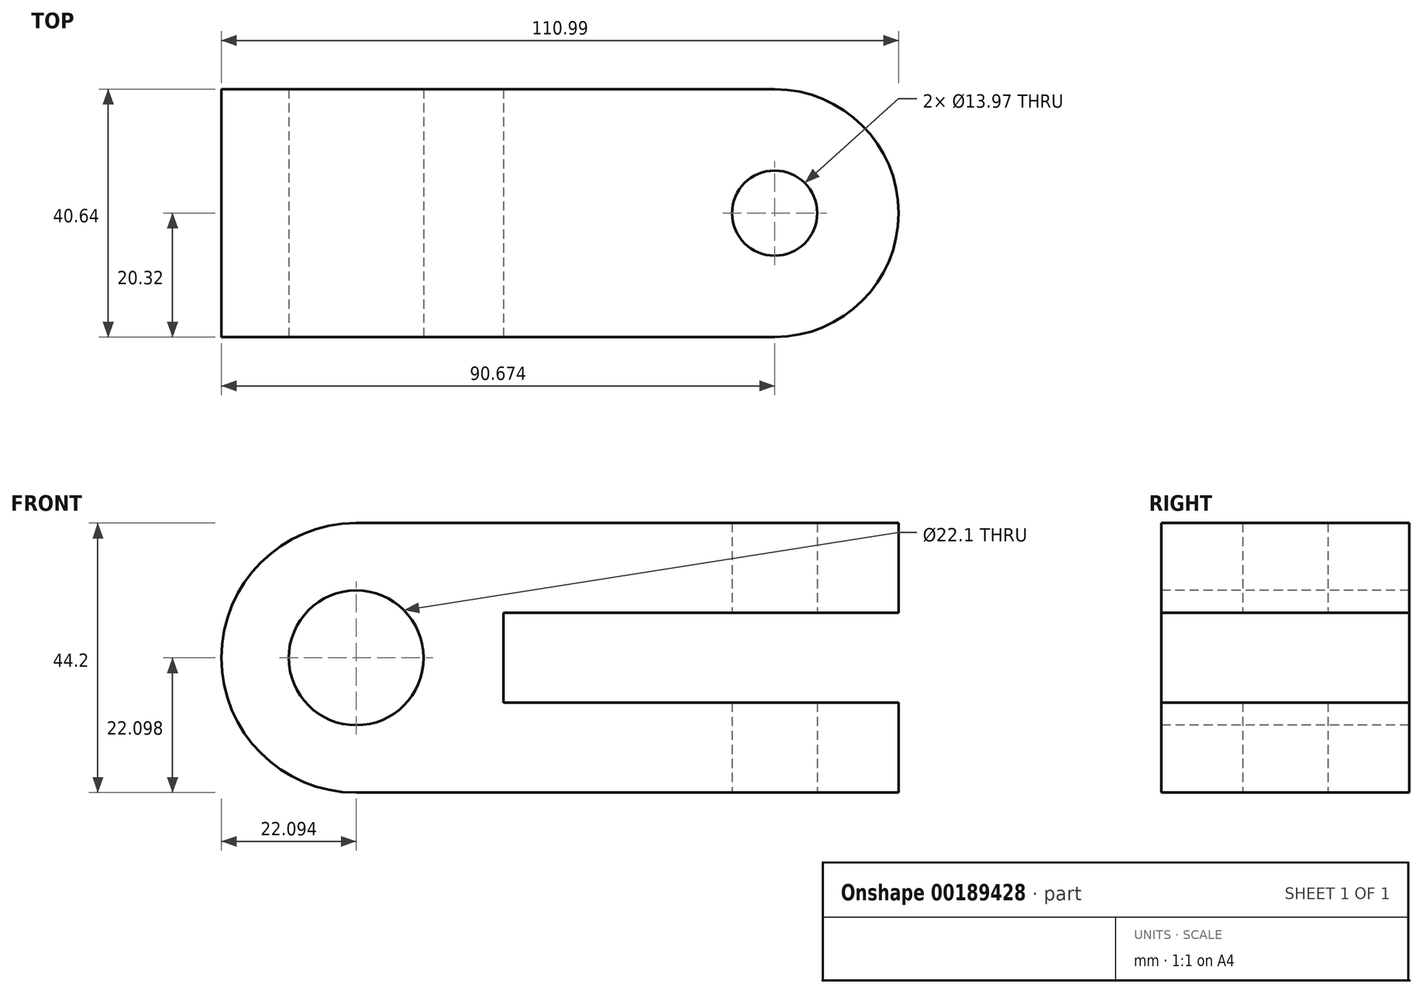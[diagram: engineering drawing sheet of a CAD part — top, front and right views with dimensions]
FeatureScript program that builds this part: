
annotation { "Feature Type Name" : "Feature", "Feature Type Description" : "" }
export const myFeature = defineFeature(function(context is Context, id is Id, definition is map)
    precondition{}
    {
        {
            var Q0;
            Q0=qCreatedBy(makeId("Top.planeOp"),FACE);
            var sketch = newSketch(context, id + "F0", { "sketchPlane" : qUnion([Q0])});
            skLineSegment(sketch, "E0.bottom", {"start": v(-36.36, 20.32) * mm, "end": v(32.22, 20.32) * mm});
            skLineSegment(sketch, "E0.top", {"start": v(-36.36, -20.32) * mm, "end": v(32.22, -20.32) * mm});
            skLineSegment(sketch, "E0.left", {"start": v(-36.36, 20.32) * mm, "end": v(-36.36, -20.32) * mm});
            skLineSegment(sketch, "E0.right", {"start": v(32.22, 20.32) * mm, "end": v(32.22, -20.32) * mm});
            skPoint(sketch, "E0.middle", {"position": v(-2.07, 0) * mm});
            skArc(sketch, "E1", {"start": v(32.22, -20.32) * mm, "mid": v(52.54, 0) * mm, "end": v(32.22, 20.32) * mm});
            skCircle(sketch, "E2", {"center": v(32.22, 0) * mm, "radius": 6.99 * mm});
            skSolve(sketch);
        }
        {
            var Q0;
            Q0=qCreatedBy(makeId("Front.planeOp"),FACE);
            var sketch = newSketch(context, id + "F1", { "sketchPlane" : qUnion([Q0])});
            skLineSegment(sketch, "E3.bottom", {"start": v(52.54, 29.46) * mm, "end": v(-12.23, 29.46) * mm});
            skLineSegment(sketch, "E3.top", {"start": v(52.54, 14.73) * mm, "end": v(-12.23, 14.73) * mm});
            skLineSegment(sketch, "E3.left", {"start": v(52.54, 29.46) * mm, "end": v(52.54, 14.73) * mm});
            skLineSegment(sketch, "E3.right", {"start": v(-12.23, 29.46) * mm, "end": v(-12.23, 14.73) * mm});
            skSolve(sketch);
        }
        {
            var Q0;
            Q0=qCreatedBy(makeId("Front.planeOp"),FACE);
            var sketch = newSketch(context, id + "F2", { "sketchPlane" : qUnion([Q0])});
            skCircle(sketch, "E4", {"center": v(-36.36, 22.1) * mm, "radius": 11.05 * mm});
            skCircle(sketch, "E5.0", {"center": v(-36.36, 22.1) * mm, "radius": 22.1 * mm});
            skSolve(sketch);
        }
        {
            var Q0;
            {var subQ2=sQuery(id+"F0.wireOp",EDGE,"E0.bottom");Q0=makeQuery(id+"F0.imprint","IMPRINT",FACE,{"disambiguationData":[TD([[makeQuery(id+"F0.imprint","IMPRINT",EDGE,{"derivedFrom":subQ2}),-1.0]])]});}
            var Q1;
            {var subQ0=sQuery(id+"F0.wireOp",EDGE,"E1");Q1=makeQuery(id+"F0.imprint","IMPRINT",FACE,{"disambiguationData":[TD([[makeQuery(id+"F0.imprint","IMPRINT",EDGE,{"derivedFrom":subQ0}),1.0]])]});}
            extrude(context, id + "F3", {"entities" : qUnion([Q0, Q1]), "depth" : 44.2 * mm});
        }
        {
            var Q0;
            Q0 = qSketchRegion(id + "F1", true);
            var Q1;
            Q1=makeQuery(id+"F2.imprint","IMPRINT",FACE,{"disambiguationData":[TD([[makeQuery(id+"F2.imprint","IMPRINT",EDGE,{"derivedFrom":sQuery(id+"F2.wireOp",EDGE,"E4")}),1.0]])]});
            extrude(context, id + "F4", {"entities" : qUnion([Q0, Q1]), "operationType" : NewBodyOperationType.REMOVE, "endBound" : BoundingType.SYMMETRIC, "oppositeDirection" : true, "depth" : 50.8 * mm});
        }
        {
            var Q0;
            Q0=makeQuery(id+"F2.imprint","IMPRINT",FACE,{"disambiguationData":[TD([[makeQuery(id+"F2.imprint","IMPRINT",EDGE,{"derivedFrom":sQuery(id+"F2.wireOp",EDGE,"E4")}),-1.0]])]});
            extrude(context, id + "F5", {"entities" : qUnion([Q0]), "operationType" : NewBodyOperationType.ADD, "endBound" : BoundingType.SYMMETRIC, "depth" : 40.64 * mm});
        }
    });
